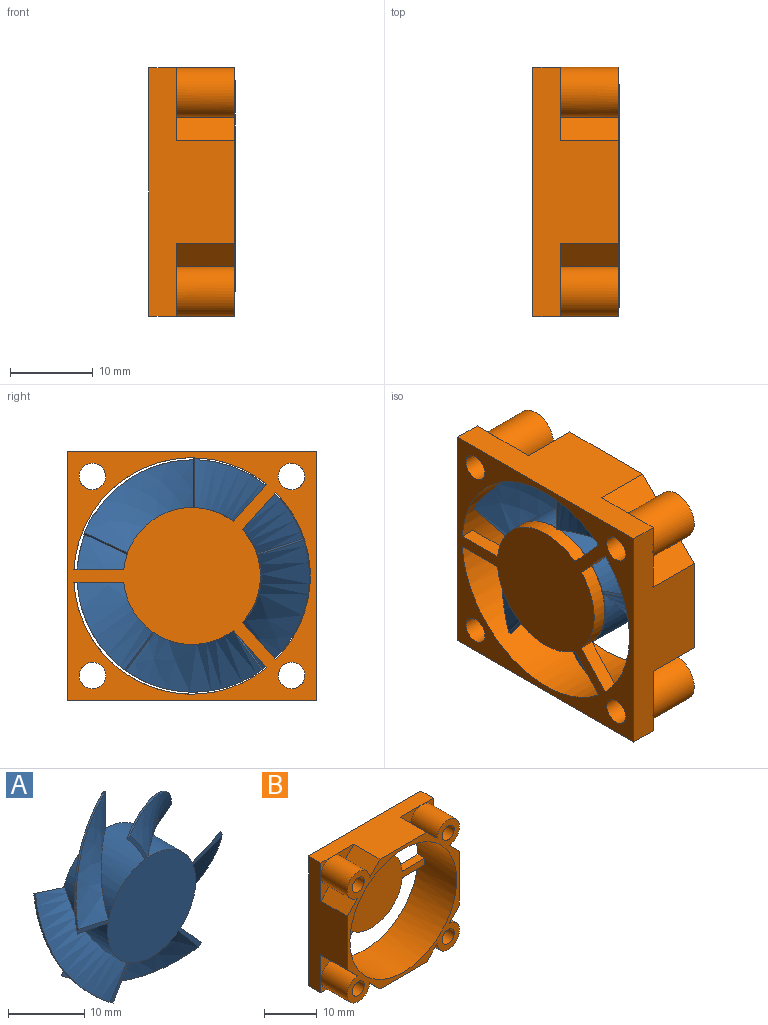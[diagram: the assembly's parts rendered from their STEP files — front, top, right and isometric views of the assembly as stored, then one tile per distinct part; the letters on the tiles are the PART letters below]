
ASSEMBLY  parts=2 mates=1
PART A: 33 faces, bbox 28.7x11.4x29.1 mm
  f0: cylinder r=8.2mm len=14.98mm, axis (0,1,0), area 80.2mm2, adj f9,f12,f13,f18,f26
  f1: bspline ~18.33x12.17mm, area 111mm2, adj f2,f13,f17,f18,f19,f20,f22,f23
  f2: bspline ~2.5x1.41mm, area 0.8mm2, adj f1,f3,f20,f23
  f3: bspline ~17.18x11.57mm, area 108.1mm2, adj f2,f13,f16,f20,f22,f23
  f4: bspline ~16.32x9.33mm, area 97.6mm2, adj f10,f13,f15,f24
  f5: bspline ~16.87x9.18mm, area 100.4mm2, adj f10,f13,f16,f24
  f6: bspline ~19.88x10mm, area 97.6mm2, adj f11,f13,f14,f25
  f7: bspline ~19.83x10mm, area 100.4mm2, adj f11,f13,f15,f25
  f8: bspline ~17.89x12.15mm, area 100.4mm2, adj f12,f13,f14,f21
  f9: bspline ~18.01x12.99mm, area 97.6mm2, adj f0,f12,f13,f21
  f10: plane 4.8x3.56mm, normal (-0.64,0.61,-0.46), area 1.7mm2, adj f4,f5,f15,f24
  f11: plane 4.8x3.56mm, normal (-0.64,0.61,0.46), area 1.7mm2, adj f6,f7,f14,f25
  f12: plane 5.58x1.97mm, normal (0.24,0.61,0.75), area 1.7mm2, adj f0,f8,f9,f21
  f13: plane 26.91x25.47mm, normal (0,-1,0), area 228.4mm2, adj f0,f1,f3,f4,f5,f6,f7,f8
  f14: cylinder r=8.2mm len=13.24mm, axis (0,1,0), area 84.4mm2, adj f6,f8,f11,f13,f18
  f15: cylinder r=8.2mm len=13.02mm, axis (0,1,0), area 84.4mm2, adj f4,f7,f10,f13,f18
  f16: cylinder r=8.2mm len=14.83mm, axis (0,1,0), area 88.5mm2, adj f3,f5,f13,f18
  f17: cylinder r=8.2mm len=15.63mm, axis (0,1,0), area 84.3mm2, adj f1,f13,f18,f28
  f18: plane 16.4x16.4mm, normal (0,1,0), area 211mm2, adj f0,f1,f14,f15,f16,f17,f19,f26
  f19: bspline ~3.75x3.43mm, area 0.1mm2, adj f1,f18,f20
  f20: plane 6.21x2.88mm, normal (0.24,0.61,-0.75), area 1.9mm2, adj f1,f2,f3,f19
  f21: cylinder r=14mm len=16.54mm, axis (0,-1,0), area 6mm2, adj f8,f9,f12,f13
  f22: cylinder r=14mm len=16.86mm, axis (0,-1,0), area 6mm2, adj f1,f3,f13,f23
  f23: plane 0.7x0.42mm, normal (0,-1,0), area 0.1mm2, adj f1,f2,f3,f22
  f24: cylinder r=14mm len=16.97mm, axis (0,-1,0), area 6mm2, adj f4,f5,f10,f13
  f25: cylinder r=14mm len=17.62mm, axis (0,-1,0), area 6mm2, adj f6,f7,f11,f13
  f26: bspline ~14.38x14.07mm, area 103.3mm2, adj f0,f13,f18,f27,f29,f30,f31,f32
  f27: bspline ~0.49x0.47mm, area 0.1mm2, adj f18,f26,f30
  f28: bspline ~14.2x14.2mm, area 100.4mm2, adj f13,f17,f30,f31
  f29: bspline ~0.72x0.47mm, area 0.1mm2, adj f26,f30,f32
  f30: plane 6.19x0.24mm, normal (0.79,0.61,0), area 1.8mm2, adj f26,f27,f28,f29,f32
  f31: cylinder r=14mm len=13.79mm, axis (0,-1,0), area 6.1mm2, adj f13,f26,f28,f32
  f32: plane 0.72x0.22mm, normal (0,-1,0), area 0.1mm2, adj f26,f29,f30,f31
PART B: 45 faces, bbox 30x10.3x30 mm
  f0: plane 5.79x2.79mm, normal (0,-1,0), area 5.8mm2, adj f11,f21,f32
  f1: plane 3x3mm, normal (0,-1,0), area 1.9mm2, adj f11,f15,f32
  f2: plane 5.79x2.79mm, normal (0,-1,0), area 5.8mm2, adj f15,f31,f32
  f3: plane 5.79x2.79mm, normal (0,-1,0), area 5.8mm2, adj f15,f29,f30
  f4: plane 3x3mm, normal (0,-1,0), area 1.9mm2, adj f13,f15,f29
  f5: plane 5.79x2.79mm, normal (0,-1,0), area 5.8mm2, adj f13,f26,f27
  f6: plane 3x3mm, normal (0,-1,0), area 1.9mm2, adj f12,f13,f26
  f7: plane 5.79x2.79mm, normal (0,-1,0), area 5.8mm2, adj f12,f25,f26
  f8: plane 5.79x2.79mm, normal (0,-1,0), area 5.8mm2, adj f12,f23,f24
  f9: plane 5.79x2.79mm, normal (0,-1,0), area 5.8mm2, adj f13,f28,f29
  f10: plane 3x3mm, normal (0,-1,0), area 1.9mm2, adj f11,f12,f23
  f11: plane 30x10.3mm, normal (-1,0,0), area 186mm2, adj f0,f1,f10,f12,f15,f20,f21,f22
  f12: plane 30x10.3mm, normal (0,0,-1), area 186mm2, adj f6,f7,f8,f10,f11,f13,f24,f25
  f13: plane 30x10.3mm, normal (1,0,0), area 186mm2, adj f4,f5,f6,f9,f12,f15,f27,f28
  f14: cylinder r=1.6mm len=10.3mm, axis (0,1,0), area 103.5mm2, adj f33,f44
  f15: plane 30x10.3mm, normal (0,0,1), area 186mm2, adj f1,f2,f3,f4,f11,f13,f30,f31
  f16: cylinder r=14.25mm len=28.5mm, axis (0,1,0), area 914.1mm2, adj f33,f35,f36,f38,f39,f41,f42,f43
  f17: cylinder r=1.6mm len=10.3mm, axis (0,1,0), area 103.5mm2, adj f33,f44
  f18: cylinder r=1.6mm len=10.3mm, axis (0,1,0), area 103.5mm2, adj f33,f44
  f19: cylinder r=1.6mm len=10.3mm, axis (0,1,0), area 103.5mm2, adj f33,f44
  f20: plane 5.79x2.79mm, normal (0,-1,0), area 5.8mm2, adj f11,f22,f23
  f21: plane 7x2.79mm, normal (-0.71,0,0.71), area 27.7mm2, adj f0,f11,f32,f33
  f22: plane 7x2.79mm, normal (-0.71,0,-0.71), area 27.7mm2, adj f11,f20,f23,f33
  f23: cylinder r=3mm len=7mm, axis (0,1,0), area 96.1mm2, adj f8,f10,f20,f22,f24,f33
  f24: plane 7x2.79mm, normal (-0.71,0,-0.71), area 27.7mm2, adj f8,f12,f23,f33
  f25: plane 7x2.79mm, normal (0.71,0,-0.71), area 27.7mm2, adj f7,f12,f26,f33
  f26: cylinder r=3mm len=7mm, axis (0,1,0), area 96.1mm2, adj f5,f6,f7,f25,f27,f33
  f27: plane 7x2.79mm, normal (0.71,0,-0.71), area 27.7mm2, adj f5,f13,f26,f33
  f28: plane 7x2.79mm, normal (0.71,0,0.71), area 27.7mm2, adj f9,f13,f29,f33
  f29: cylinder r=3mm len=7mm, axis (0,1,0), area 96.1mm2, adj f3,f4,f9,f28,f30,f33
  f30: plane 7x2.79mm, normal (0.71,0,0.71), area 27.7mm2, adj f3,f15,f29,f33
  f31: plane 7x2.79mm, normal (-0.71,0,0.71), area 27.7mm2, adj f2,f15,f32,f33
  f32: cylinder r=3mm len=7mm, axis (0,1,0), area 96.1mm2, adj f0,f1,f2,f21,f31,f33
  f33: plane 30x30mm, normal (0,-1,0), area 175.7mm2, adj f11,f12,f13,f14,f15,f16,f17,f18
  f34: cylinder r=8.25mm len=11.18mm, axis (0,1,0), area 22.1mm2, adj f35,f42,f43,f44
  f35: plane 4.46x4.03mm, normal (-0.74,0,-0.67), area 10.8mm2, adj f16,f34,f43,f44
  f36: plane 4.46x4.03mm, normal (0.74,0,0.67), area 10.8mm2, adj f16,f37,f43,f44
  f37: cylinder r=8.25mm len=13.17mm, axis (0,1,0), area 31.5mm2, adj f36,f38,f43,f44
  f38: plane 6.01x1.8mm, normal (0,0,1), area 10.8mm2, adj f16,f37,f43,f44
  f39: plane 6.01x1.8mm, normal (0,0,-1), area 10.8mm2, adj f16,f40,f43,f44
  f40: cylinder r=8.25mm len=13.17mm, axis (0,1,0), area 31.5mm2, adj f39,f41,f43,f44
  f41: plane 4.46x4.03mm, normal (0.74,0,-0.67), area 10.8mm2, adj f16,f40,f43,f44
  f42: plane 4.46x4.03mm, normal (-0.74,0,0.67), area 10.8mm2, adj f16,f34,f43,f44
  f43: plane 24.35x22.11mm, normal (0,-1,0), area 240.8mm2, adj f16,f34,f35,f36,f37,f38,f39,f40
  f44: plane 30x30mm, normal (0,1,0), area 470.7mm2, adj f11,f12,f13,f14,f15,f16,f17,f18
PLACE A rot(axis=(0,0,1),90deg) t=(-11.62,-14.5,28.93)mm
PLACE B rot(axis=(0,0,1),90deg) t=(-11.62,-14.35,28.93)mm
MATE revolute A.f0 <-> B.f43  axis (-1,0,0) through (1.88,-14.5,43.93)mm
